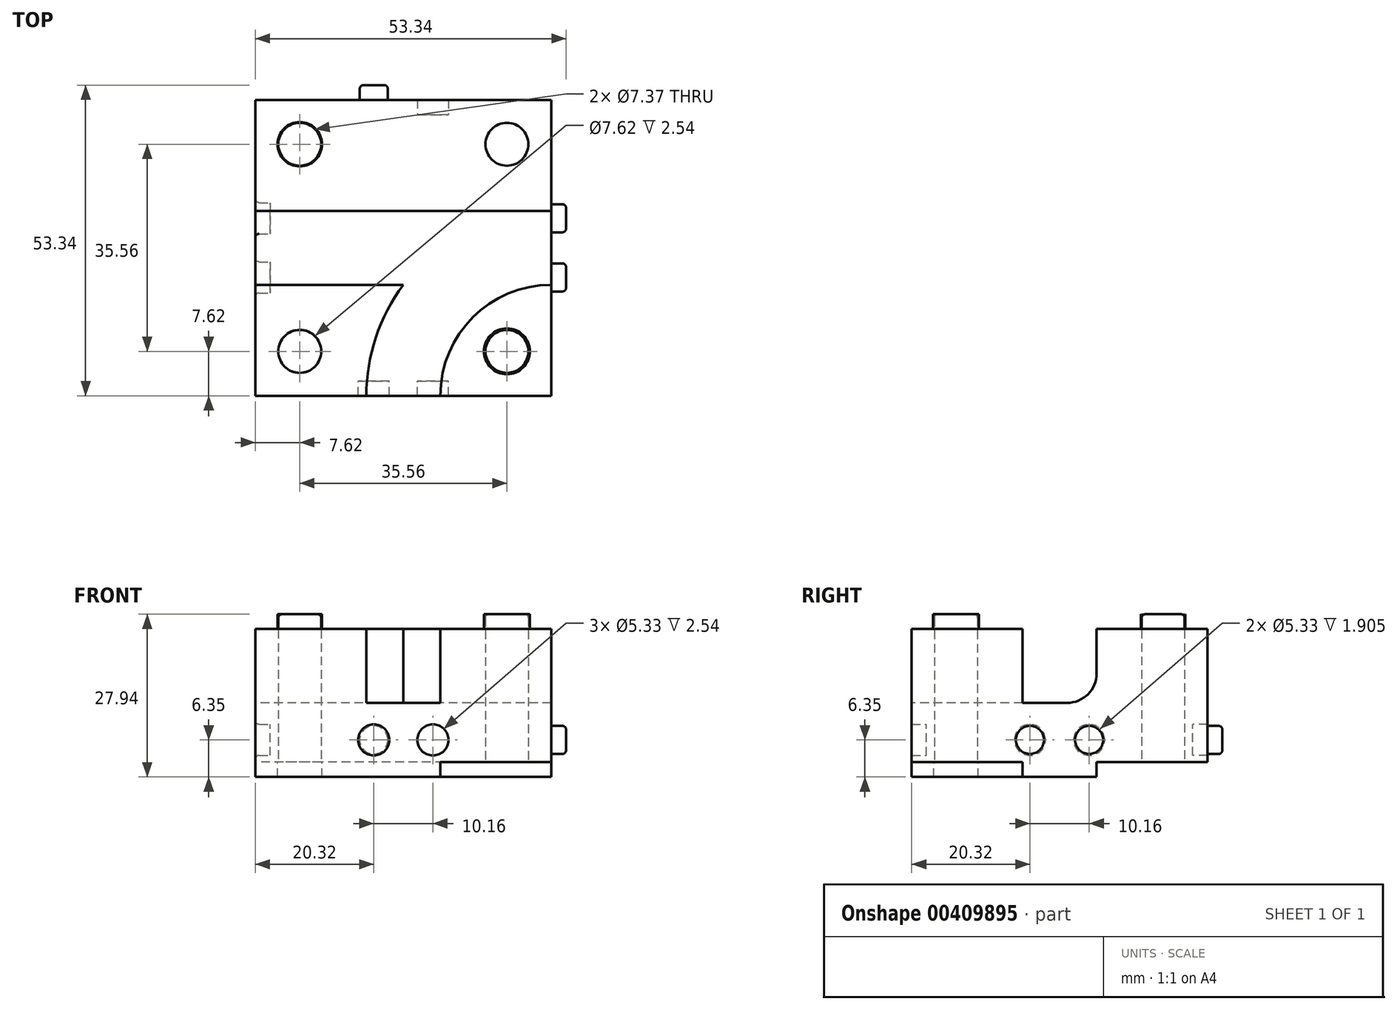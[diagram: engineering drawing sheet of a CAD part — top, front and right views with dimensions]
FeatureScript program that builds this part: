
annotation { "Feature Type Name" : "Feature", "Feature Type Description" : "" }
export const myFeature = defineFeature(function(context is Context, id is Id, definition is map)
    precondition{}
    {
        {
            var Q0;
            Q0=qCreatedBy(makeId("Top.planeOp"),FACE);
            var sketch = newSketch(context, id + "F0", { "sketchPlane" : qUnion([Q0])});
            skLineSegment(sketch, "E0.bottom", {"start": v(25.4, 25.4) * mm, "end": v(-25.4, 25.4) * mm});
            skLineSegment(sketch, "E0.top", {"start": v(25.4, -25.4) * mm, "end": v(-25.4, -25.4) * mm});
            skLineSegment(sketch, "E0.left", {"start": v(25.4, 25.4) * mm, "end": v(25.4, -25.4) * mm});
            skLineSegment(sketch, "E0.right", {"start": v(-25.4, 25.4) * mm, "end": v(-25.4, -25.4) * mm});
            skPoint(sketch, "E1", {"position": v(17.78, 17.78) * mm});
            skPoint(sketch, "E2", {"position": v(17.78, 25.4) * mm});
            skLineSegment(sketch, "E3", {"start": v(17.78, 17.78) * mm, "end": v(17.78, 25.4) * mm, "construction": true});
            skCircle(sketch, "E4", {"center": v(17.78, 17.78) * mm, "radius": 3.81 * mm, "construction": true});
            skCircle(sketch, "E5.MirrorC", {"center": v(-17.78, 17.78) * mm, "radius": 3.81 * mm});
            skCircle(sketch, "E6.MirrorC", {"center": v(-17.78, -17.78) * mm, "radius": 3.81 * mm});
            skPoint(sketch, "E7", {"position": v(25.4, 0) * mm});
            skPoint(sketch, "E8", {"position": v(-25.4, 0) * mm});
            skCircle(sketch, "E9", {"center": v(17.78, 17.78) * mm, "radius": 3.68 * mm});
            skCircle(sketch, "E10.MirrorC", {"center": v(-17.78, 17.78) * mm, "radius": 3.68 * mm});
            skCircle(sketch, "E11.MirrorC", {"center": v(-17.78, -17.78) * mm, "radius": 3.68 * mm});
            skLineSegment(sketch, "E12", {"start": v(-25.4, 0) * mm, "end": v(25.4, 0) * mm, "construction": true});
            skLineSegment(sketch, "E13", {"start": v(0, 25.4) * mm, "end": v(0, -25.4) * mm, "construction": true});
            skCircle(sketch, "E14", {"center": v(17.78, 17.78) * mm, "radius": 3.94 * mm});
            skLineSegment(sketch, "E15", {"start": v(17.78, 21.46) * mm, "end": v(17.78, 21.72) * mm});
            skPoint(sketch, "E15.endSnap0", {"position": v(17.78, 21.6) * mm});
            skLineSegment(sketch, "E16", {"start": v(25.4, 6.35) * mm, "end": v(25.4, -6.35) * mm});
            skPoint(sketch, "E17", {"position": v(6.35, -25.4) * mm});
            skPoint(sketch, "E18", {"position": v(-6.35, -25.4) * mm});
            skArc(sketch, "E19", {"start": v(6.35, -25.4) * mm, "mid": v(11.93, -11.93) * mm, "end": v(25.4, -6.35) * mm});
            skArc(sketch, "E20", {"start": v(-6.35, -25.4) * mm, "mid": v(-4.72, -15.36) * mm, "end": v(0, -6.35) * mm});
            skLineSegment(sketch, "E21", {"start": v(25.4, 6.35) * mm, "end": v(-25.4, 6.35) * mm});
            skLineSegment(sketch, "E22", {"start": v(25.4, -6.35) * mm, "end": v(0, -6.35) * mm, "construction": true});
            skLineSegment(sketch, "E23", {"start": v(0, -6.35) * mm, "end": v(-25.4, -6.35) * mm});
            skPoint(sketch, "E24", {"position": v(0, 0) * mm});
            skCircle(sketch, "E25", {"center": v(0, 0) * mm, "radius": 5.08 * mm});
            skCircle(sketch, "E26", {"center": v(0, 0) * mm, "radius": 2.54 * mm, "construction": true});
            skPoint(sketch, "E27", {"position": v(0, 5.08) * mm});
            skPoint(sketch, "E28", {"position": v(0, 2.54) * mm});
            skPoint(sketch, "E29", {"position": v(2.54, 0) * mm});
            skPoint(sketch, "E30", {"position": v(2.67, 0) * mm});
            skPoint(sketch, "E31", {"position": v(2.41, 0) * mm});
            skLineSegment(sketch, "E32", {"start": v(2.41, 0) * mm, "end": v(2.67, 0) * mm, "construction": true});
            skCircle(sketch, "E33", {"center": v(0, 0) * mm, "radius": 2.41 * mm});
            skCircle(sketch, "E34", {"center": v(0, 0) * mm, "radius": 2.67 * mm});
            skLineSegment(sketch, "E35", {"start": v(17.78, 17.78) * mm, "end": v(25.4, 17.78) * mm, "construction": true});
            skCircle(sketch, "E36.MirrorC", {"center": v(17.78, -17.78) * mm, "radius": 3.94 * mm});
            skCircle(sketch, "E37.MirrorC", {"center": v(17.78, -17.78) * mm, "radius": 3.68 * mm});
            skSolve(sketch);
        }
        {
            var Q0;
            Q0=makeQuery(id+"F0.imprint","IMPRINT",FACE,{"disambiguationData":[TD([[makeQuery(id+"F0.imprint","IMPRINT",EDGE,{"derivedFrom":sQuery(id+"F0.wireOp",EDGE,"E5.MirrorC")}),1.0]])]});
            var Q1;
            Q1=makeQuery(id+"F0.imprint","IMPRINT",FACE,{"disambiguationData":[TD([[makeQuery(id+"F0.imprint","IMPRINT",EDGE,{"derivedFrom":sQuery(id+"F0.wireOp",EDGE,"E5.MirrorC")}),-1.0]])]});
            var Q2;
            Q2=makeQuery(id+"F0.imprint","IMPRINT",FACE,{"disambiguationData":[TD([[makeQuery(id+"F0.imprint","IMPRINT",EDGE,{"derivedFrom":sQuery(id+"F0.wireOp",EDGE,"E6.MirrorC")}),1.0]])]});
            var Q3;
            {var subQ0=sQuery(id+"F0.wireOp",EDGE,"E13");var subQ1=sQuery(id+"F0.wireOp",EDGE,"E0.top");var subQ2=makeQuery(id+"F0.imprint","INTERSECT",VERTEX,{"derivedFrom":[subQ1,subQ0]});Q3=makeQuery(id+"F0.imprint","IMPRINT",FACE,{"disambiguationData":[TD([[makeQuery(id+"F0.imprint","IMPRINT",EDGE,{"disambiguationData":[TD([[subQ2,-1.0]])],"derivedFrom":subQ1}),-1.0]])]});}
            var Q4;
            {var subQ0=sQuery(id+"F0.wireOp",EDGE,"E13");var subQ1=sQuery(id+"F0.wireOp",EDGE,"E0.top");var subQ2=makeQuery(id+"F0.imprint","INTERSECT",VERTEX,{"derivedFrom":[subQ1,subQ0]});Q4=makeQuery(id+"F0.imprint","IMPRINT",FACE,{"disambiguationData":[TD([[makeQuery(id+"F0.imprint","IMPRINT",EDGE,{"disambiguationData":[TD([[subQ2,1.0]])],"derivedFrom":subQ1}),-1.0]])]});}
            var Q5;
            Q5=makeQuery(id+"F0.imprint","IMPRINT",FACE,{"disambiguationData":[TD([[makeQuery(id+"F0.imprint","IMPRINT",EDGE,{"derivedFrom":sQuery(id+"F0.wireOp",EDGE,"E10.MirrorC")}),-1.0]])]});
            var Q6;
            Q6=makeQuery(id+"F0.imprint","IMPRINT",FACE,{"disambiguationData":[TD([[makeQuery(id+"F0.imprint","IMPRINT",EDGE,{"derivedFrom":sQuery(id+"F0.wireOp",EDGE,"E9")}),-1.0]])]});
            var Q7;
            Q7=makeQuery(id+"F0.imprint","IMPRINT",FACE,{"disambiguationData":[TD([[makeQuery(id+"F0.imprint","IMPRINT",EDGE,{"derivedFrom":sQuery(id+"F0.wireOp",EDGE,"E9")}),1.0]])]});
            var Q8;
            Q8=makeQuery(id+"F0.imprint","IMPRINT",FACE,{"disambiguationData":[TD([[makeQuery(id+"F0.imprint","IMPRINT",EDGE,{"derivedFrom":sQuery(id+"F0.wireOp",EDGE,"E11.MirrorC")}),1.0]])]});
            var Q9;
            Q9=makeQuery(id+"F0.imprint","IMPRINT",FACE,{"disambiguationData":[TD([[makeQuery(id+"F0.imprint","IMPRINT",EDGE,{"derivedFrom":sQuery(id+"F0.wireOp",EDGE,"E6.MirrorC")}),-1.0]])]});
            var Q10;
            Q10=makeQuery(id+"F0.imprint","IMPRINT",FACE,{"disambiguationData":[TD([[makeQuery(id+"F0.imprint","IMPRINT",EDGE,{"derivedFrom":sQuery(id+"F0.wireOp",EDGE,"E36.MirrorC")}),-1.0]])]});
            var Q11;
            Q11=makeQuery(id+"F0.imprint","IMPRINT",FACE,{"disambiguationData":[TD([[makeQuery(id+"F0.imprint","IMPRINT",EDGE,{"derivedFrom":sQuery(id+"F0.wireOp",EDGE,"E37.MirrorC")}),-1.0]])]});
            extrude(context, id + "F1", {"entities" : qUnion([Q0, Q1, Q2, Q3, Q4, Q5, Q6, Q7, Q8, Q9, Q10, Q11]), "depth" : 12.7 * mm});
        }
        {
            var Q0;
            Q0=makeQuery(id+"F0.imprint","IMPRINT",FACE,{"disambiguationData":[TD([[makeQuery(id+"F0.imprint","IMPRINT",EDGE,{"derivedFrom":sQuery(id+"F0.wireOp",EDGE,"E11.MirrorC")}),1.0]])]});
            var Q1;
            Q1=makeQuery(id+"F0.imprint","IMPRINT",FACE,{"disambiguationData":[TD([[makeQuery(id+"F0.imprint","IMPRINT",EDGE,{"derivedFrom":sQuery(id+"F0.wireOp",EDGE,"E10.MirrorC")}),-1.0]])]});
            var Q2;
            Q2=makeQuery(id+"F0.imprint","IMPRINT",FACE,{"disambiguationData":[TD([[makeQuery(id+"F0.imprint","IMPRINT",EDGE,{"derivedFrom":sQuery(id+"F0.wireOp",EDGE,"E9")}),1.0]])]});
            var Q3;
            Q3=makeQuery(id+"F0.imprint","IMPRINT",FACE,{"disambiguationData":[TD([[makeQuery(id+"F0.imprint","IMPRINT",EDGE,{"derivedFrom":sQuery(id+"F0.wireOp",EDGE,"E37.MirrorC")}),-1.0]])]});
            extrude(context, id + "F2", {"entities" : qUnion([Q0, Q1, Q2, Q3]), "operationType" : NewBodyOperationType.ADD, "depth" : 15.24 * mm});
        }
        {
            var Q0;
            Q0=makeQuery(id+"F0.imprint","IMPRINT",FACE,{"disambiguationData":[TD([[makeQuery(id+"F0.imprint","IMPRINT",EDGE,{"derivedFrom":sQuery(id+"F0.wireOp",EDGE,"E6.MirrorC")}),-1.0]])]});
            var Q1;
            {var subQ1=sQuery(id+"F0.wireOp",EDGE,"E0.bottom");Q1=makeQuery(id+"F0.imprint","IMPRINT",FACE,{"disambiguationData":[TD([[makeQuery(id+"F0.imprint","IMPRINT",EDGE,{"derivedFrom":subQ1}),1.0]])]});}
            var Q2;
            Q2=makeQuery(id+"F0.imprint","IMPRINT",FACE,{"disambiguationData":[TD([[makeQuery(id+"F0.imprint","IMPRINT",EDGE,{"derivedFrom":sQuery(id+"F0.wireOp",EDGE,"E16")}),-1.0]])]});
            var Q3;
            Q3=makeQuery(id+"F1.opExtrude","CAP_FACE",FACE,{"disambiguationData":[OSD([sQuery(id+"F0.wireOp",EDGE,"E0.bottom"),sQuery(id+"F0.wireOp",EDGE,"E0.left"),sQuery(id+"F0.wireOp",EDGE,"E0.right"),sQuery(id+"F0.wireOp",EDGE,"lMXQf7WU-VQvn-eUw7-3v8j-XpuHpQXpMMjl"),sQuery(id+"F0.wireOp",EDGE,"E10.MirrorC"),sQuery(id+"F0.wireOp",EDGE,"E14"),sQuery(id+"F0.wireOp",EDGE,"E21")])],"isStart":false});
            var Q4;
            Q4=makeQuery(id+"F0.imprint","IMPRINT",FACE,{"disambiguationData":[TD([[makeQuery(id+"F0.imprint","IMPRINT",EDGE,{"derivedFrom":sQuery(id+"F0.wireOp",EDGE,"E25")}),1.0]])]});
            var Q5;
            Q5=makeQuery(id+"F0.imprint","IMPRINT",FACE,{"disambiguationData":[TD([[makeQuery(id+"F0.imprint","IMPRINT",EDGE,{"derivedFrom":sQuery(id+"F0.wireOp",EDGE,"E33")}),1.0]])]});
            var Q6;
            Q6=makeQuery(id+"F0.imprint","IMPRINT",FACE,{"disambiguationData":[TD([[makeQuery(id+"F0.imprint","IMPRINT",EDGE,{"derivedFrom":sQuery(id+"F0.wireOp",EDGE,"E33")}),-1.0]])]});
            var Q7;
            Q7=makeQuery(id+"F0.imprint","IMPRINT",FACE,{"disambiguationData":[TD([[makeQuery(id+"F0.imprint","IMPRINT",EDGE,{"derivedFrom":sQuery(id+"F0.wireOp",EDGE,"E6.MirrorC")}),1.0]])]});
            var Q8;
            Q8=makeQuery(id+"F0.imprint","IMPRINT",FACE,{"disambiguationData":[TD([[makeQuery(id+"F0.imprint","IMPRINT",EDGE,{"derivedFrom":sQuery(id+"F0.wireOp",EDGE,"E11.MirrorC")}),1.0]])]});
            var Q9;
            Q9=makeQuery(id+"F0.imprint","IMPRINT",FACE,{"disambiguationData":[TD([[makeQuery(id+"F0.imprint","IMPRINT",EDGE,{"derivedFrom":sQuery(id+"F0.wireOp",EDGE,"E10.MirrorC")}),-1.0]])]});
            var Q10;
            Q10=makeQuery(id+"F0.imprint","IMPRINT",FACE,{"disambiguationData":[TD([[makeQuery(id+"F0.imprint","IMPRINT",EDGE,{"derivedFrom":sQuery(id+"F0.wireOp",EDGE,"E5.MirrorC")}),-1.0]])]});
            var Q11;
            Q11=makeQuery(id+"F0.imprint","IMPRINT",FACE,{"disambiguationData":[TD([[makeQuery(id+"F0.imprint","IMPRINT",EDGE,{"derivedFrom":sQuery(id+"F0.wireOp",EDGE,"E9")}),-1.0]])]});
            var Q12;
            Q12=makeQuery(id+"F0.imprint","IMPRINT",FACE,{"disambiguationData":[TD([[makeQuery(id+"F0.imprint","IMPRINT",EDGE,{"derivedFrom":sQuery(id+"F0.wireOp",EDGE,"E9")}),1.0]])]});
            var Q13;
            Q13=makeQuery(id+"F0.imprint","IMPRINT",FACE,{"disambiguationData":[TD([[makeQuery(id+"F0.imprint","IMPRINT",EDGE,{"derivedFrom":sQuery(id+"F0.wireOp",EDGE,"E37.MirrorC")}),-1.0]])]});
            var Q14;
            Q14=makeQuery(id+"F0.imprint","IMPRINT",FACE,{"disambiguationData":[TD([[makeQuery(id+"F0.imprint","IMPRINT",EDGE,{"derivedFrom":sQuery(id+"F0.wireOp",EDGE,"E36.MirrorC")}),-1.0]])]});
            var Q15;
            {var subQ3=sQuery(id+"F0.wireOp",EDGE,"E19");Q15=makeQuery(id+"F0.imprint","IMPRINT",FACE,{"disambiguationData":[TD([[makeQuery(id+"F0.imprint","IMPRINT",EDGE,{"derivedFrom":subQ3}),-1.0]])]});}
            extrude(context, id + "F3", {"entities" : qUnion([Q0, Q1, Q2, Q3, Q4, Q5, Q6, Q7, Q8, Q9, Q10, Q11, Q12, Q13, Q14, Q15]), "operationType" : NewBodyOperationType.ADD, "oppositeDirection" : true, "depth" : 12.7 * mm});
        }
        {
            var Q0;
            Q0=makeQuery(id+"F0.imprint","IMPRINT",FACE,{"disambiguationData":[TD([[makeQuery(id+"F0.imprint","IMPRINT",EDGE,{"derivedFrom":sQuery(id+"F0.wireOp",EDGE,"E6.MirrorC")}),1.0]])]});
            var Q1;
            Q1=makeQuery(id+"F0.imprint","IMPRINT",FACE,{"disambiguationData":[TD([[makeQuery(id+"F0.imprint","IMPRINT",EDGE,{"derivedFrom":sQuery(id+"F0.wireOp",EDGE,"E11.MirrorC")}),1.0]])]});
            var Q2;
            Q2=makeQuery(id+"F0.imprint","IMPRINT",FACE,{"disambiguationData":[TD([[makeQuery(id+"F0.imprint","IMPRINT",EDGE,{"derivedFrom":sQuery(id+"F0.wireOp",EDGE,"E5.MirrorC")}),-1.0]])]});
            var Q3;
            Q3=makeQuery(id+"F0.imprint","IMPRINT",FACE,{"disambiguationData":[TD([[makeQuery(id+"F0.imprint","IMPRINT",EDGE,{"derivedFrom":sQuery(id+"F0.wireOp",EDGE,"E10.MirrorC")}),-1.0]])]});
            var Q4;
            Q4=makeQuery(id+"F0.imprint","IMPRINT",FACE,{"disambiguationData":[TD([[makeQuery(id+"F0.imprint","IMPRINT",EDGE,{"derivedFrom":sQuery(id+"F0.wireOp",EDGE,"E9")}),1.0]])]});
            var Q5;
            Q5=makeQuery(id+"F0.imprint","IMPRINT",FACE,{"disambiguationData":[TD([[makeQuery(id+"F0.imprint","IMPRINT",EDGE,{"derivedFrom":sQuery(id+"F0.wireOp",EDGE,"E37.MirrorC")}),-1.0]])]});
            var Q6;
            Q6=makeQuery(id+"F0.imprint","IMPRINT",FACE,{"disambiguationData":[TD([[makeQuery(id+"F0.imprint","IMPRINT",EDGE,{"derivedFrom":sQuery(id+"F0.wireOp",EDGE,"E36.MirrorC")}),-1.0]])]});
            var Q7;
            Q7=makeQuery(id+"F0.imprint","IMPRINT",FACE,{"disambiguationData":[TD([[makeQuery(id+"F0.imprint","IMPRINT",EDGE,{"derivedFrom":sQuery(id+"F0.wireOp",EDGE,"E9")}),-1.0]])]});
            extrude(context, id + "F4", {"entities" : qUnion([Q0, Q1, Q2, Q3, Q4, Q5, Q6, Q7]), "operationType" : NewBodyOperationType.REMOVE, "oppositeDirection" : true, "depth" : 12.7 * mm, "hasSecondDirection" : true, "secondDirectionOppositeDirection" : true, "secondDirectionDepth" : 10.16 * mm});
        }
        {
            var Q0;
            Q0=qCreatedBy(makeId("Right.planeOp"),FACE);
            var sketch = newSketch(context, id + "F5", { "sketchPlane" : qUnion([Q0])});
            skLineSegment(sketch, "E38", {"start": v(-25.4, 12.7) * mm, "end": v(-25.4, -12.7) * mm, "construction": true});
            skPoint(sketch, "E39", {"position": v(-25.4, 0) * mm});
            skPoint(sketch, "E40", {"position": v(-25.4, -6.35) * mm});
            skPoint(sketch, "E41", {"position": v(-5.08, -6.35) * mm});
            skPoint(sketch, "E42", {"position": v(-2.67, -6.35) * mm});
            skPoint(sketch, "E43", {"position": v(-2.41, -6.35) * mm});
            skPoint(sketch, "E44", {"position": v(2.41, -6.35) * mm});
            skPoint(sketch, "E45", {"position": v(2.67, -6.35) * mm});
            skPoint(sketch, "E46", {"position": v(5.08, -6.35) * mm});
            skCircle(sketch, "E47", {"center": v(-5.08, -6.35) * mm, "radius": 2.41 * mm});
            skCircle(sketch, "E48", {"center": v(-5.08, -6.35) * mm, "radius": 2.67 * mm});
            skCircle(sketch, "E49", {"center": v(5.08, -6.35) * mm, "radius": 2.41 * mm});
            skCircle(sketch, "E50", {"center": v(5.08, -6.35) * mm, "radius": 2.67 * mm});
            skLineSegment(sketch, "E51", {"start": v(25.4, 12.7) * mm, "end": v(25.4, -12.7) * mm});
            skPoint(sketch, "E52", {"position": v(25.4, 0) * mm});
            skPoint(sketch, "E53", {"position": v(25.4, -6.35) * mm});
            skLineSegment(sketch, "E54", {"start": v(-2.67, 0) * mm, "end": v(-5.08, 0) * mm});
            skLineSegment(sketch, "E55", {"start": v(5.08, 0) * mm, "end": v(2.67, 0) * mm});
            skLineSegment(sketch, "E56", {"start": v(-2.41, 0) * mm, "end": v(-2.67, 0) * mm});
            skLineSegment(sketch, "E57", {"start": v(2.67, 0) * mm, "end": v(2.41, 0) * mm});
            skSolve(sketch);
        }
        {
            var Q0;
            Q0=qCreatedBy(makeId("Front.planeOp"),FACE);
            var sketch = newSketch(context, id + "F6", { "sketchPlane" : qUnion([Q0])});
            skLineSegment(sketch, "E58", {"start": v(-25.4, -12.7) * mm, "end": v(-25.4, 12.7) * mm, "construction": true});
            skLineSegment(sketch, "E59", {"start": v(25.4, -12.7) * mm, "end": v(25.4, 0) * mm, "construction": true});
            skPoint(sketch, "E60", {"position": v(25.4, -6.35) * mm});
            skPoint(sketch, "E61", {"position": v(-25.4, 0) * mm});
            skPoint(sketch, "E62", {"position": v(-25.4, -6.35) * mm});
            skPoint(sketch, "E63", {"position": v(5.08, -6.35) * mm});
            skPoint(sketch, "E64", {"position": v(2.67, -6.35) * mm});
            skPoint(sketch, "E65", {"position": v(2.41, -6.35) * mm});
            skPoint(sketch, "E66", {"position": v(-2.41, -6.35) * mm});
            skPoint(sketch, "E67", {"position": v(-2.67, -6.35) * mm});
            skPoint(sketch, "E68", {"position": v(-5.08, -6.35) * mm});
            skCircle(sketch, "E69", {"center": v(5.08, -6.35) * mm, "radius": 2.41 * mm});
            skCircle(sketch, "E70", {"center": v(5.08, -6.35) * mm, "radius": 2.67 * mm});
            skCircle(sketch, "E71", {"center": v(-5.08, -6.35) * mm, "radius": 2.67 * mm});
            skCircle(sketch, "E72", {"center": v(-5.08, -6.35) * mm, "radius": 2.41 * mm});
            skLineSegment(sketch, "E73", {"start": v(-2.67, 0) * mm, "end": v(-5.08, 0) * mm});
            skLineSegment(sketch, "E74", {"start": v(5.08, 0) * mm, "end": v(2.67, 0) * mm});
            skLineSegment(sketch, "E75", {"start": v(-2.41, 0) * mm, "end": v(-2.67, 0) * mm});
            skLineSegment(sketch, "E76", {"start": v(2.67, 0) * mm, "end": v(2.41, 0) * mm});
            skSolve(sketch);
        }
        {
            var Q0;
            Q0=makeQuery(id+"F6.imprint","IMPRINT",FACE,{"disambiguationData":[TD([[makeQuery(id+"F6.imprint","IMPRINT",EDGE,{"derivedFrom":sQuery(id+"F6.wireOp",EDGE,"E72")}),1.0]])]});
            extrude(context, id + "F7", {"entities" : qUnion([Q0]), "operationType" : NewBodyOperationType.ADD, "oppositeDirection" : true, "depth" : 27.94 * mm, "hasSecondDirection" : true, "secondDirectionOppositeDirection" : true, "secondDirectionDepth" : 22.86 * mm});
        }
        {
            var Q0;
            Q0=makeQuery(id+"F6.imprint","IMPRINT",FACE,{"disambiguationData":[TD([[makeQuery(id+"F6.imprint","IMPRINT",EDGE,{"derivedFrom":sQuery(id+"F6.wireOp",EDGE,"E72")}),1.0]])]});
            var Q1;
            Q1=makeQuery(id+"F6.imprint","IMPRINT",FACE,{"disambiguationData":[TD([[makeQuery(id+"F6.imprint","IMPRINT",EDGE,{"derivedFrom":sQuery(id+"F6.wireOp",EDGE,"E69")}),1.0]])]});
            var Q2;
            Q2=makeQuery(id+"F6.imprint","IMPRINT",FACE,{"disambiguationData":[TD([[makeQuery(id+"F6.imprint","IMPRINT",EDGE,{"derivedFrom":sQuery(id+"F6.wireOp",EDGE,"E71")}),1.0]])]});
            var Q3;
            Q3=makeQuery(id+"F6.imprint","IMPRINT",FACE,{"disambiguationData":[TD([[makeQuery(id+"F6.imprint","IMPRINT",EDGE,{"derivedFrom":sQuery(id+"F6.wireOp",EDGE,"E69")}),-1.0]])]});
            extrude(context, id + "F8", {"entities" : qUnion([Q0, Q1, Q2, Q3]), "operationType" : NewBodyOperationType.REMOVE, "depth" : 27.94 * mm, "hasSecondDirection" : true, "secondDirectionOppositeDirection" : false, "secondDirectionDepth" : 22.86 * mm});
        }
        {
            var Q0;
            Q0=makeQuery(id+"F5.imprint","IMPRINT",FACE,{"disambiguationData":[TD([[makeQuery(id+"F5.imprint","IMPRINT",EDGE,{"derivedFrom":sQuery(id+"F5.wireOp",EDGE,"E47")}),1.0]])]});
            var Q1;
            Q1=makeQuery(id+"F5.imprint","IMPRINT",FACE,{"disambiguationData":[TD([[makeQuery(id+"F5.imprint","IMPRINT",EDGE,{"derivedFrom":sQuery(id+"F5.wireOp",EDGE,"E49")}),1.0]])]});
            extrude(context, id + "F9", {"entities" : qUnion([Q0, Q1]), "operationType" : NewBodyOperationType.ADD, "depth" : 27.94 * mm, "hasSecondDirection" : true, "secondDirectionOppositeDirection" : false, "secondDirectionDepth" : 22.86 * mm});
        }
        {
            var Q0;
            Q0=makeQuery(id+"F5.imprint","IMPRINT",FACE,{"disambiguationData":[TD([[makeQuery(id+"F5.imprint","IMPRINT",EDGE,{"derivedFrom":sQuery(id+"F5.wireOp",EDGE,"E47")}),-1.0]])]});
            var Q1;
            Q1=makeQuery(id+"F5.imprint","IMPRINT",FACE,{"disambiguationData":[TD([[makeQuery(id+"F5.imprint","IMPRINT",EDGE,{"derivedFrom":sQuery(id+"F5.wireOp",EDGE,"E47")}),1.0]])]});
            var Q2;
            Q2=makeQuery(id+"F5.imprint","IMPRINT",FACE,{"disambiguationData":[TD([[makeQuery(id+"F5.imprint","IMPRINT",EDGE,{"derivedFrom":sQuery(id+"F5.wireOp",EDGE,"E49")}),1.0]])]});
            var Q3;
            Q3=makeQuery(id+"F5.imprint","IMPRINT",FACE,{"disambiguationData":[TD([[makeQuery(id+"F5.imprint","IMPRINT",EDGE,{"derivedFrom":sQuery(id+"F5.wireOp",EDGE,"E49")}),-1.0]])]});
            extrude(context, id + "F10", {"entities" : qUnion([Q0, Q1, Q2, Q3]), "operationType" : NewBodyOperationType.REMOVE, "oppositeDirection" : true, "depth" : 27.94 * mm, "hasSecondDirection" : true, "secondDirectionOppositeDirection" : true, "secondDirectionDepth" : 22.86 * mm});
        }
        {
            var Q0;
            Q0=makeQuery(id+"F6.imprint","IMPRINT",FACE,{"disambiguationData":[TD([[makeQuery(id+"F6.imprint","IMPRINT",EDGE,{"derivedFrom":sQuery(id+"F6.wireOp",EDGE,"E69")}),1.0]])]});
            var Q1;
            Q1=makeQuery(id+"F6.imprint","IMPRINT",FACE,{"disambiguationData":[TD([[makeQuery(id+"F6.imprint","IMPRINT",EDGE,{"derivedFrom":sQuery(id+"F6.wireOp",EDGE,"E69")}),-1.0]])]});
            extrude(context, id + "F11", {"entities" : qUnion([Q0, Q1]), "operationType" : NewBodyOperationType.REMOVE, "oppositeDirection" : true, "depth" : 27.94 * mm, "hasSecondDirection" : true, "secondDirectionOppositeDirection" : true, "secondDirectionDepth" : 22.86 * mm});
        }
        {
            var Q0;
            Q0=makeQuery(id+"F1.opExtrude","CAP_EDGE",EDGE,{"disambiguationData":[OSD([sQuery(id+"F0.wireOp",EDGE,"E19")])],"isStart":true});
            var Q1;
            Q1=makeQuery(id+"F1.opExtrude","CAP_EDGE",EDGE,{"disambiguationData":[OSD([sQuery(id+"F0.wireOp",EDGE,"E21")])],"isStart":true});
            var Q2;
            Q2=makeQuery(id+"F1.opExtrude","CAP_EDGE",EDGE,{"disambiguationData":[OSD([sQuery(id+"F0.wireOp",EDGE,"E20")])],"isStart":true});
            var Q3;
            Q3=makeQuery(id+"F1.opExtrude","CAP_EDGE",EDGE,{"disambiguationData":[OSD([sQuery(id+"F0.wireOp",EDGE,"E23")])],"isStart":true});
            fillet(context, id + "F12", {"entities" : qUnion([Q0, Q1, Q2, Q3]), "radius" : 5.08 * mm, "tangentPropagation" : true, "allowEdgeOverflow" : false});
        }
        {
            var Q0;
            Q0=makeQuery(id+"F2.opExtrude","CAP_EDGE",EDGE,{"disambiguationData":[OSD([sQuery(id+"F0.wireOp",EDGE,"E11.MirrorC")])],"isStart":false});
            var Q1;
            Q1=makeQuery(id+"F2.opExtrude","CAP_EDGE",EDGE,{"disambiguationData":[OSD([sQuery(id+"F0.wireOp",EDGE,"E10.MirrorC")])],"isStart":false});
            var Q2;
            Q2=makeQuery(id+"F7.opExtrude","CAP_EDGE",EDGE,{"disambiguationData":[OSD([sQuery(id+"F6.wireOp",EDGE,"E72")])],"isStart":false});
            var Q3;
            {var subQ0=sQuery(id+"F0.wireOp",EDGE,"E0.right");Q3=makeQuery(id+"F10.boolean.opBoolean","INTERSECT",EDGE,{"derivedFrom":[makeQuery(id+"FVeaqIvGeaTVGBi_11.opBoolean","MERGE",FACE,{"derivedFrom":[makeQuery(id+"F1.opExtrude","SWEPT_FACE",FACE,{"disambiguationData":[OSD([subQ0])]}),makeQuery(id+"F3.opExtrude","SWEPT_FACE",FACE,{"disambiguationData":[OSD([subQ0])]})]}),makeQuery(id+"F10.opExtrude","SWEPT_FACE",FACE,{"disambiguationData":[OSD([sQuery(id+"F5.wireOp",EDGE,"E48")])]})]});}
            var Q4;
            {var subQ0=sQuery(id+"F0.wireOp",EDGE,"E0.top");Q4=makeQuery(id+"F11.boolean.opBoolean","INTERSECT",EDGE,{"derivedFrom":[makeQuery(id+"FVeaqIvGeaTVGBi_11.opBoolean","MERGE",FACE,{"derivedFrom":[makeQuery(id+"F1.opExtrude","SWEPT_FACE",FACE,{"disambiguationData":[OSD([subQ0])]}),makeQuery(id+"F3.opExtrude","SWEPT_FACE",FACE,{"disambiguationData":[OSD([subQ0])]})]}),makeQuery(id+"F11.opExtrude","SWEPT_FACE",FACE,{"disambiguationData":[OSD([sQuery(id+"F6.wireOp",EDGE,"E70")])]})]});}
            var Q5;
            Q5=makeQuery(id+"F9.opExtrude","CAP_EDGE",EDGE,{"disambiguationData":[OSD([sQuery(id+"F5.wireOp",EDGE,"E49")])],"isStart":false});
            var Q6;
            Q6=makeQuery(id+"F9.opExtrude","CAP_EDGE",EDGE,{"disambiguationData":[OSD([sQuery(id+"F5.wireOp",EDGE,"E47")])],"isStart":false});
            var Q7;
            {var subQ0=sQuery(id+"F0.wireOp",EDGE,"lMXQf7WU-VQvn-eUw7-3v8j-XpuHpQXpMMjl");var subQ1=sQuery(id+"F0.wireOp",EDGE,"E0.bottom");Q7=makeQuery(id+"F8.boolean.opBoolean","INTERSECT",EDGE,{"derivedFrom":[makeQuery(id+"FVeaqIvGeaTVGBi_11.opBoolean","MERGE",FACE,{"derivedFrom":[makeQuery(id+"F1.opExtrude","SWEPT_FACE",FACE,{"disambiguationData":[OSD([subQ1,subQ0])]}),makeQuery(id+"F1.opExtrude","SWEPT_FACE",FACE,{"disambiguationData":[OSD([subQ1])]}),makeQuery(id+"F3.opExtrude","SWEPT_FACE",FACE,{"disambiguationData":[OSD([subQ1,subQ0])]})]}),makeQuery(id+"F8.opExtrude","SWEPT_FACE",FACE,{"disambiguationData":[OSD([sQuery(id+"F6.wireOp",EDGE,"E70")])]})]});}
            var Q8;
            {var subQ0=sQuery(id+"F0.wireOp",EDGE,"lMXQf7WU-VQvn-eUw7-3v8j-XpuHpQXpMMjl");var subQ1=sQuery(id+"F0.wireOp",EDGE,"E0.bottom");Q8=makeQuery(id+"F8.boolean.opBoolean","INTERSECT",EDGE,{"derivedFrom":[makeQuery(id+"FVeaqIvGeaTVGBi_11.opBoolean","MERGE",FACE,{"derivedFrom":[makeQuery(id+"F1.opExtrude","SWEPT_FACE",FACE,{"disambiguationData":[OSD([subQ1,subQ0])]}),makeQuery(id+"F1.opExtrude","SWEPT_FACE",FACE,{"disambiguationData":[OSD([subQ1])]}),makeQuery(id+"F3.opExtrude","SWEPT_FACE",FACE,{"disambiguationData":[OSD([subQ1,subQ0])]})]}),makeQuery(id+"F8.opExtrude","SWEPT_FACE",FACE,{"disambiguationData":[OSD([sQuery(id+"F6.wireOp",EDGE,"E71")])]})]});}
            var Q9;
            {var subQ0=sQuery(id+"F0.wireOp",EDGE,"E0.right");Q9=makeQuery(id+"F10.boolean.opBoolean","INTERSECT",EDGE,{"derivedFrom":[makeQuery(id+"FVeaqIvGeaTVGBi_11.opBoolean","MERGE",FACE,{"derivedFrom":[makeQuery(id+"F1.opExtrude","SWEPT_FACE",FACE,{"disambiguationData":[OSD([subQ0]),TDD([makeQuery(id+"F0.imprint","IMPRINT",EDGE,{"disambiguationData":[TD([[makeQuery(id+"F0.imprint","INTERSECT",VERTEX,{"derivedFrom":[sQuery(id+"F0.wireOp",EDGE,"E0.bottom"),subQ0]}),-1.0]])],"derivedFrom":subQ0})])]}),makeQuery(id+"F1.opExtrude","SWEPT_FACE",FACE,{"disambiguationData":[OSD([subQ0]),TDD([makeQuery(id+"F0.imprint","IMPRINT",EDGE,{"disambiguationData":[TD([[makeQuery(id+"F0.imprint","INTERSECT",VERTEX,{"derivedFrom":[sQuery(id+"F0.wireOp",EDGE,"E0.top"),subQ0]}),1.0]])],"derivedFrom":subQ0})])]}),makeQuery(id+"F3.opExtrude","SWEPT_FACE",FACE,{"disambiguationData":[OSD([subQ0])]})]}),makeQuery(id+"F10.opExtrude","SWEPT_FACE",FACE,{"disambiguationData":[OSD([sQuery(id+"F5.wireOp",EDGE,"E50")])]})]});}
            var Q10;
            Q10=makeQuery(id+"F2.opExtrude","CAP_EDGE",EDGE,{"disambiguationData":[OSD([sQuery(id+"F0.wireOp",EDGE,"E9")])],"isStart":false});
            var Q11;
            Q11=makeQuery(id+"F2.opExtrude","CAP_EDGE",EDGE,{"disambiguationData":[OSD([sQuery(id+"F0.wireOp",EDGE,"E37.MirrorC")])],"isStart":false});
            var Q12;
            Q12=makeQuery(id+"F4.boolean.opBoolean","COPY",EDGE,{"derivedFrom":makeQuery(id+"F4.opExtrude","CAP_EDGE",EDGE,{"disambiguationData":[OSD([sQuery(id+"F0.wireOp",EDGE,"E36.MirrorC")])],"isStart":false})});
            var Q13;
            Q13=makeQuery(id+"F4.boolean.opBoolean","COPY",EDGE,{"derivedFrom":makeQuery(id+"F4.opExtrude","CAP_EDGE",EDGE,{"disambiguationData":[OSD([sQuery(id+"F0.wireOp",EDGE,"E14")])],"isStart":false})});
            var Q14;
            Q14=makeQuery(id+"F4.boolean.opBoolean","COPY",EDGE,{"derivedFrom":makeQuery(id+"F4.opExtrude","CAP_EDGE",EDGE,{"disambiguationData":[OSD([sQuery(id+"F0.wireOp",EDGE,"E5.MirrorC")])],"isStart":false})});
            var Q15;
            Q15=makeQuery(id+"F4.boolean.opBoolean","COPY",EDGE,{"derivedFrom":makeQuery(id+"F4.opExtrude","CAP_EDGE",EDGE,{"disambiguationData":[OSD([sQuery(id+"F0.wireOp",EDGE,"E6.MirrorC")])],"isStart":false})});
            fillet(context, id + "F13", {"entities" : qUnion([Q0, Q1, Q2, Q3, Q4, Q5, Q6, Q7, Q8, Q9, Q10, Q11, Q12, Q13, Q14, Q15]), "radius" : 0.64 * mm, "tangentPropagation" : true, "allowEdgeOverflow" : false});
        }
    });
